# Revit family: FILTRATION ANTI-BACTERIENNE FD2000DP
name_source: partatom
category: Equipement de génie climatique
revit_build: Autodesk Revit 2018 (Build: 20170223_1515(x64)
units: mm (PartAtom-declared; Revit-internal decimal feet)

## family parameters
Basée sur le plan de construction = Non
Classification = Aucun
Cote de connecteur circulaire = Utiliser le diamètre
Couper avec des vides une fois chargée = Non
Partagée = Non
Point de calcul de pièce = Non
Toujours verticalement = Oui
Type d'élément = Normal

## types (1)
- GABARIT
    BRANCHEMENT_TERRE = Oui
    DEBIT_MAX = 2000.0 m³/h
    DESCR_CONNECT = BRIDE DN80
    DN = 80 mm  [stored 0.262467 ft]
    Fabricant = MIL'S
    HAUTEUR = 0 mm  [stored 0 ft]
    LARGEUR = 0 mm  [stored 0 ft]
    LONGUEUR = 0 mm  [stored 0 ft]
    POIDS(Kg) = 0 mm  [stored 0 ft]
    Zone de maintenance 1 = Oui
    ØBRIDE = 200 mm  [stored 0.656168 ft]
    ØCANA = 105 mm  [stored 0.344488 ft]
    ØPORTEE_JOINT = 125 mm  [stored 0.410105 ft]

note: [stored X ft] marks values corroborated as IEEE doubles in the binary element streams (Revit-internal decimal feet)

## geometry (parser evidence)
native form markers: Sweep x3
no freeform markers — native parametric forms only
